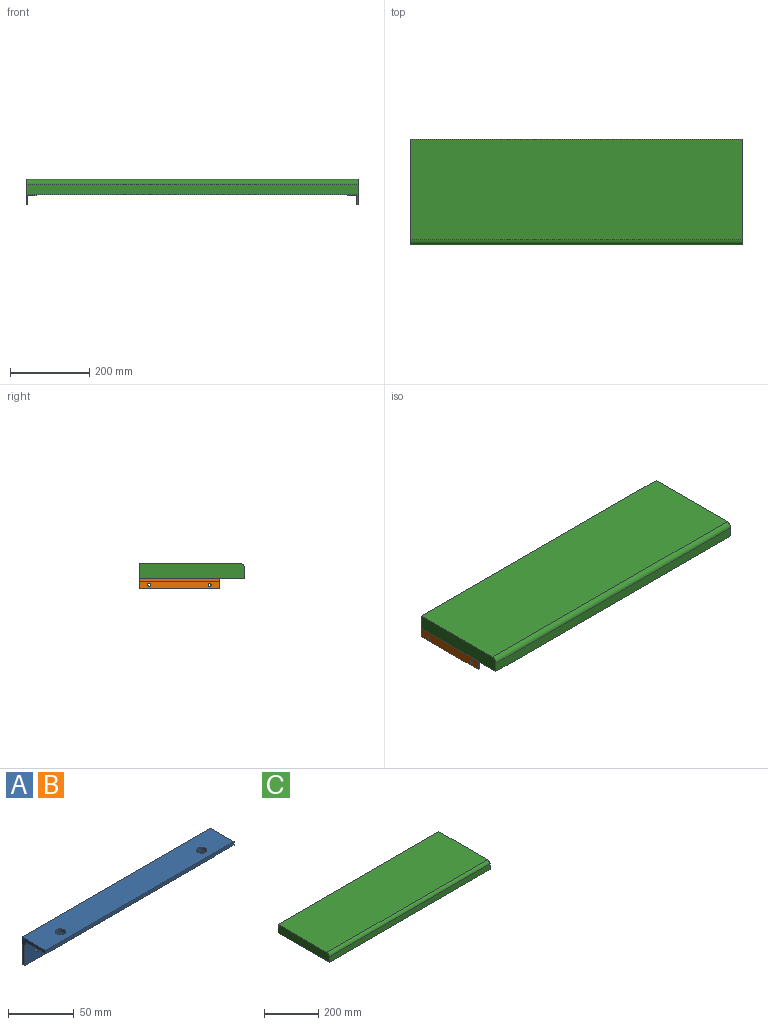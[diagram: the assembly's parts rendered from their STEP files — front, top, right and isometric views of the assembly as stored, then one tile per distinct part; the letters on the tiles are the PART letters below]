
ASSEMBLY  parts=3 mates=6
PART A: 13 faces, bbox 203.2x25.4x25.4 mm
  f0: plane 203.2x3.18mm, normal (0,0,-1), area 645.2mm2, adj f1,f6,f7,f8
  f1: plane 203.2x25.4mm, normal (0,1,0), area 5124.7mm2, adj f0,f2,f7,f8,f11,f12
  f2: plane 203.2x25.4mm, normal (0,0,1), area 5062.3mm2, adj f1,f3,f7,f8,f9,f10
  f3: plane 203.2x3.18mm, normal (0,-1,0), area 645.2mm2, adj f2,f4,f7,f8
  f4: plane 203.2x19.05mm, normal (0,0,-1), area 3772mm2, adj f3,f5,f7,f8,f9,f10
  f5: cylinder r=3.17mm len=203.2mm, axis (-1,0,0), area 1013.4mm2, adj f4,f6,f7,f8
  f6: plane 203.2x19.05mm, normal (0,-1,0), area 3834.4mm2, adj f0,f5,f7,f8,f11,f12
  f7: plane 25.4x25.4mm, normal (1,0,0), area 153.4mm2, adj f0,f1,f2,f3,f4,f5,f6
  f8: plane 25.4x25.4mm, normal (-1,0,0), area 153.4mm2, adj f0,f1,f2,f3,f4,f5,f6
  f9: cylinder r=3.97mm len=7.94mm, axis (0,0,-1), area 79.2mm2, adj f2,f4
  f10: cylinder r=3.97mm len=7.94mm, axis (0,0,-1), area 79.2mm2, adj f2,f4
  f11: cylinder r=2.41mm len=4.83mm, axis (0,-1,0), area 48.1mm2, adj f1,f6
  f12: cylinder r=2.41mm len=4.83mm, axis (0,-1,0), area 48.1mm2, adj f1,f6
PART B: same geometry as A
PART C: 7 faces, bbox 838.2x266.7x38.1 mm
  f0: plane 838.2x254mm, normal (0,0,1), area 212902.8mm2, adj f1,f4,f5,f6
  f1: cylinder r=12.7mm len=838.2mm, axis (-1,0,0), area 16721.3mm2, adj f0,f2,f5,f6
  f2: plane 838.2x25.4mm, normal (0,-1,0), area 21290.3mm2, adj f1,f3,f5,f6
  f3: plane 838.2x266.7mm, normal (0,0,-1), area 223547.9mm2, adj f2,f4,f5,f6
  f4: plane 838.2x38.1mm, normal (0,1,0), area 31935.4mm2, adj f0,f3,f5,f6
  f5: plane 266.7x38.1mm, normal (1,0,0), area 10126.7mm2, adj f0,f1,f2,f3,f4
  f6: plane 266.7x38.1mm, normal (-1,0,0), area 10126.7mm2, adj f0,f1,f2,f3,f4
PLACE A rot(axis=(0.58,0.58,0.58),120deg) t=(838.2,-203.2,-38.1)mm
PLACE B rot(axis=(0.58,-0.58,-0.58),120deg) t=(0,0,-38.1)mm
PLACE C at identity fixed
MATE planar A.f2 <-> C.f5  axis (1,0,0) through (838.2,-101.6,-50.74)mm
MATE planar B.f1 <-> C.f3  axis (0,0,1) through (12.68,-101.6,-38.1)mm
MATE planar B.f8 <-> A.f7  axis (0,1,0) through (7.46,0,-45.56)mm
MATE planar B.f8 <-> C.f4  axis (0,1,0) through (7.46,0,-45.56)mm
MATE planar B.f2 <-> C.f6  axis (-1,0,0) through (0,-101.6,-50.74)mm
MATE planar A.f1 <-> C.f3  axis (0,0,1) through (825.52,-101.6,-38.1)mm
